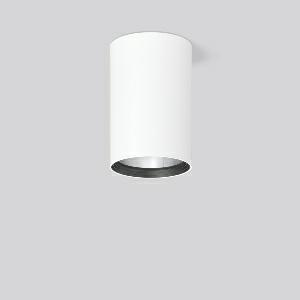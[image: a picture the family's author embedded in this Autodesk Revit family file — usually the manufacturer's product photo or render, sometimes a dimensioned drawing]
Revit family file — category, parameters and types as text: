
# Revit family: heledon_maxi_a_931219_002_2_76_f2e4
name_source: partatom
category: Lighting Fixtures
units: mm (PartAtom-declared; Revit-internal decimal feet)

## family parameters
Cut with Voids When Loaded = No
Host = Face
Light Source = No
Part Type = Normal
Room Calculation Point = No
Round Connector Dimension = Use Diameter
Shared = No

## types (1)
- HELEDON maxi A (1 x LED Modul 927, 3050 lm, 2700)
    Apparent Load = 25 VA
    Approval mark = CE
    CIE Flux Codes = 97 100 100 100 100
    Color Rendering = 92
    Color Temperature = 2700
    Default Elevation = 1800 mm
    Description = Series: HELEDON maxi
Cylindrical surface-mounted downlight. Housing: die-cast aluminium, powder-coated. Internal ceiling frame polycarbonate with bayonet mounting. Black plastic ring and recessed LED to prevent glare from the side. Optical assembly with reflector made of MIRO-Silver with 98% total light reflection for outstanding efficiency - can be changed without tools. Best colour rendering index Ra>90. Suitable for Ceiling mounting. Easy installation with a separate ceiling frame with bayonet mounting and plug connection. Driver integrated. Connected via plug-in connector. High quality converter without flickering and stroboscopic effect. The following accessories can be mounted without use of tools: interchangeable lenses, decorative glasses, honeycomb louvre, clear and frosted diffusers, white interchangeable plastic ring. 
Colour: traffic white, matt (RAL 9016)
Diameter: 123 mm
Height: 183 mm
Lamp: LED
Socket: without socket
Colour temperature: 2700K
Colour rendering index (CRI): 92
System power: 25 W
Rated luminous flux: 3050 lm
Luminous efficiency: 122 lm/W
Control gear: Converter, dimmable, DALI
Protection class: I
Type of protection: IP 20
    Height = 183 mm
    Lamp = 1 x LED Modul 927
    Lamp Light Flux = 3050 lm
    Lamp count = 1
    Length = 123 mm
    Lifetime = 50000 h
    Luminous efficacy = 122 lm/W
    Manufacturer = RZB
    ModVariant = No
    Model = 931219.002.2.76
    Mounting Place = Ceiling
    Mounting Type = Surface mounted
    Number of Poles = 1
    OnlyDefault = Yes
    Power Factor = 1
    Product Name = HELEDON maxi A
    Product group = Surface mounted downlights
    ProductGroupID = 302
    Protection Class = Protection class I
    Protection Degree = IP 20
    RLX_Detail_Level = 1
    RLX_Emergency_Light_Flux = 0 lm
    RLX_Emergency_Type = 0
    RLX_Emergency_Type_DB = No
    RlxData = <blob elided: 96233 chars, md5=2fca0f4e>
    Socket = socket
    Standby Power = 0 W
    System Light Flux = 3050 lm
    System Power = 25 W
    Type Comments = Product without accessories
    Type Image = 931192.002.jpg
    URL = http://relux.com
    VarID = ---
    Voltage = 230 V
    Voltage Range = 220-240 V
    Weight = 0.00 kg
    Width = 0 mm  [stored 0 ft]

note: [stored X ft] marks values corroborated as IEEE doubles in the binary element streams (Revit-internal decimal feet)

## geometry (parser evidence)
native form markers: Blend x4, Sweep x12
no freeform markers — native parametric forms only
